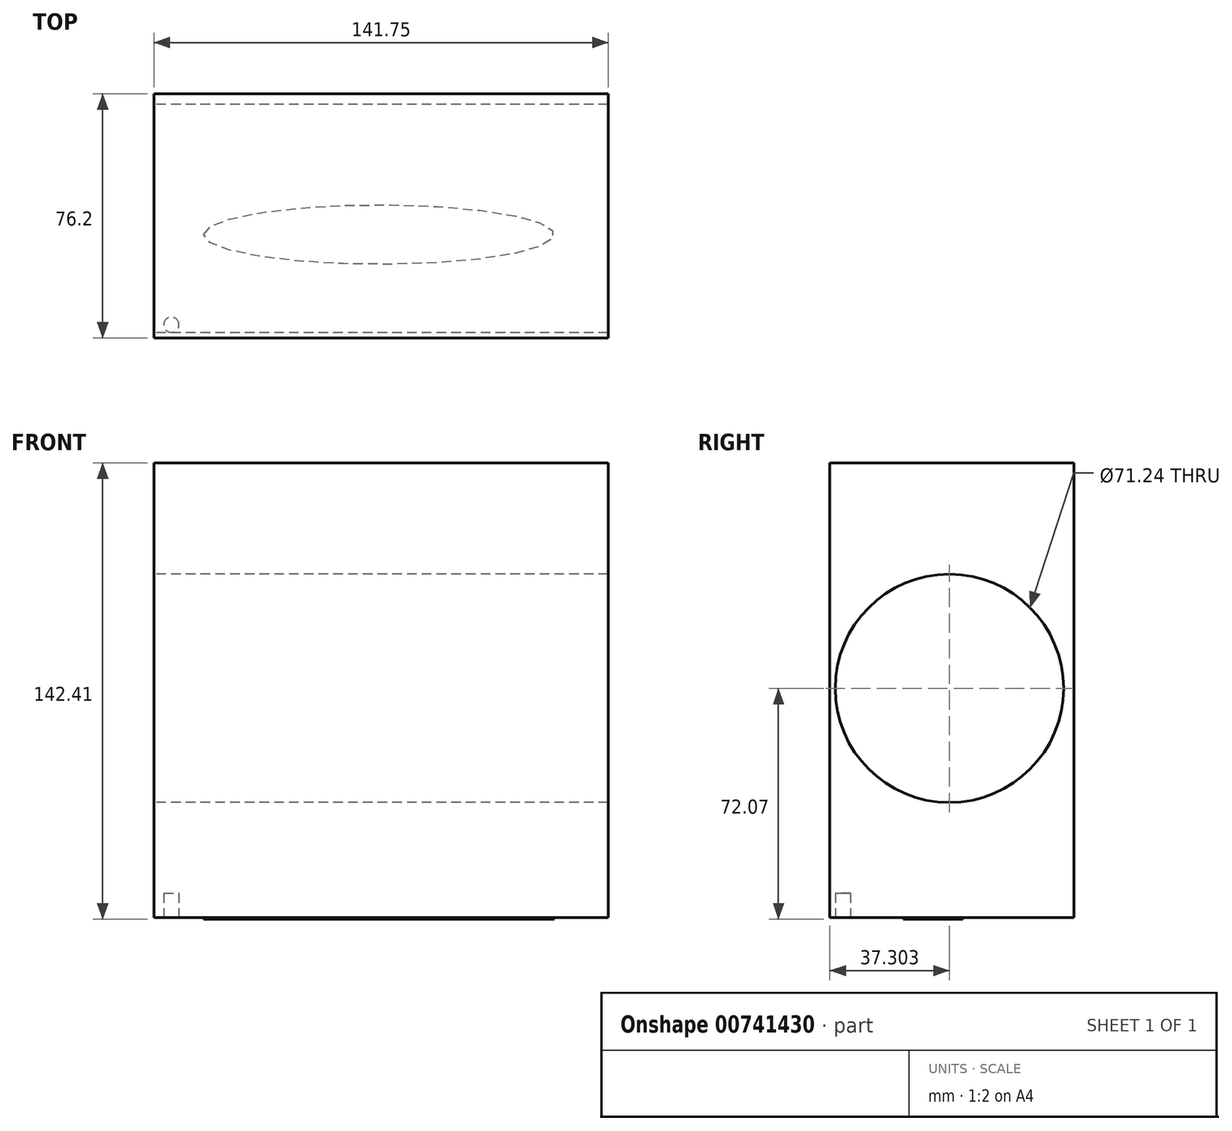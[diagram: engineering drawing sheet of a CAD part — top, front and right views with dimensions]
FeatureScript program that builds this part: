
annotation { "Feature Type Name" : "Feature", "Feature Type Description" : "" }
export const myFeature = defineFeature(function(context is Context, id is Id, definition is map)
    precondition{}
    {
        {
            var Q0;
            Q0=qCreatedBy(makeId("Front.planeOp"),FACE);
            var sketch = newSketch(context, id + "F0", { "sketchPlane" : qUnion([Q0])});
            skLineSegment(sketch, "E0.bottom", {"start": v(-70.21, 70.34) * mm, "end": v(71.54, 70.34) * mm});
            skLineSegment(sketch, "E0.top", {"start": v(-70.21, -71.56) * mm, "end": v(71.54, -71.56) * mm});
            skLineSegment(sketch, "E0.left", {"start": v(-70.21, 70.34) * mm, "end": v(-70.21, -71.56) * mm});
            skLineSegment(sketch, "E0.right", {"start": v(71.54, 70.34) * mm, "end": v(71.54, -71.56) * mm});
            skSolve(sketch);
        }
        {
            var Q0;
            Q0 = qSketchRegion(id + "F0", true);
            extrude(context, id + "F1", {"entities" : qUnion([Q0]), "depth" : 76.2 * mm, "offsetDistance" : 25.4 * mm});
        }
        {
            var Q0;
            Q0=makeQuery(id+"F1.opExtrude","SWEPT_FACE",FACE,{"disambiguationData":[OSD([sQuery(id+"F0.wireOp",EDGE,"E0.left")])]});
            var sketch = newSketch(context, id + "F2", { "sketchPlane" : qUnion([Q0])});
            skCircle(sketch, "E1", {"center": v(38.9, 0) * mm, "radius": 35.62 * mm});
            skSolve(sketch);
        }
        {
            var Q0;
            Q0 = qSketchRegion(id + "F2", true);
            extrude(context, id + "F3", {"entities" : qUnion([Q0]), "operationType" : NewBodyOperationType.REMOVE, "oppositeDirection" : true, "depth" : 152.4 * mm, "offsetDistance" : 25.4 * mm});
        }
        {
            var Q0;
            Q0=makeQuery(id+"F1.opExtrude","SWEPT_FACE",FACE,{"disambiguationData":[OSD([sQuery(id+"F0.wireOp",EDGE,"E0.top")])]});
            var sketch = newSketch(context, id + "F4", { "sketchPlane" : qUnion([Q0])});
            skEllipse(sketch, "E2", {"center": v(0, 43.94) * mm, "majorRadius": 54.65 * mm, "minorRadius": 9.28 * mm, "majorAxis": v(-1, 0)});
            skSolve(sketch);
        }
        {
            var Q0;
            Q0 = qSketchRegion(id + "F4", true);
            extrude(context, id + "F5", {"entities" : qUnion([Q0]), "operationType" : NewBodyOperationType.ADD, "depth" : 0.5 * mm, "offsetDistance" : 25.4 * mm});
        }
        {
            var Q0;
            Q0=makeQuery(id+"F1.opExtrude","SWEPT_FACE",FACE,{"disambiguationData":[OSD([sQuery(id+"F0.wireOp",EDGE,"E0.top")])]});
            var sketch = newSketch(context, id + "F6", { "sketchPlane" : qUnion([Q0])});
            skCircle(sketch, "E3", {"center": v(-64.77, 72.08) * mm, "radius": 2.38 * mm});
            skSolve(sketch);
        }
        {
            var Q0;
            Q0 = qSketchRegion(id + "F6", true);
            extrude(context, id + "F7", {"entities" : qUnion([Q0]), "operationType" : NewBodyOperationType.REMOVE, "oppositeDirection" : true, "depth" : 7.62 * mm, "offsetDistance" : 25.4 * mm});
        }
    });
